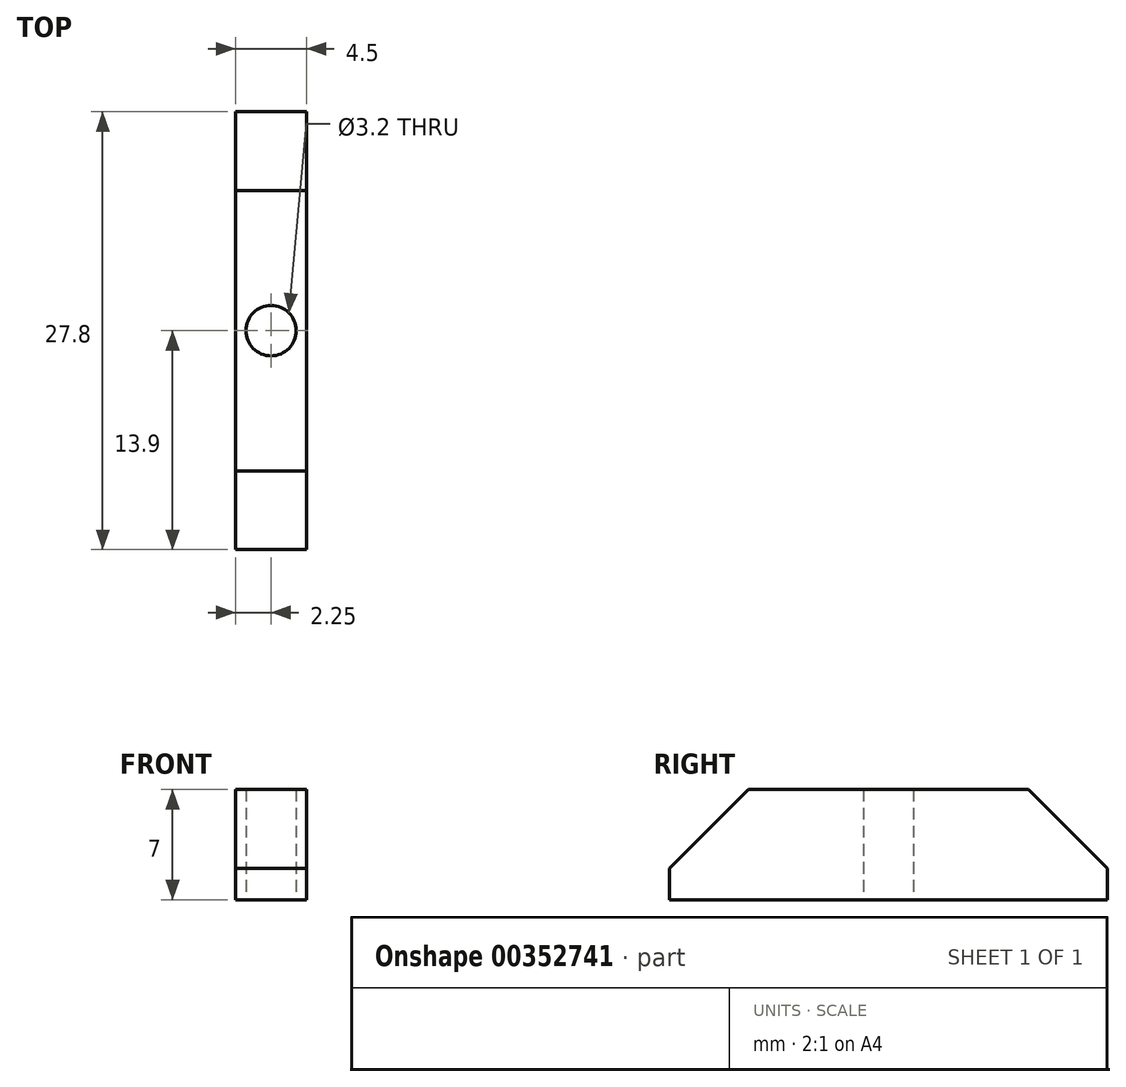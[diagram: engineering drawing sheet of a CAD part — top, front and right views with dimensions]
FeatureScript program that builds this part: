
annotation { "Feature Type Name" : "Feature", "Feature Type Description" : "" }
export const myFeature = defineFeature(function(context is Context, id is Id, definition is map)
    precondition{}
    {
        {
            var Q0;
            Q0=qCreatedBy(makeId("Top.planeOp"),FACE);
            var sketch = newSketch(context, id + "F0", { "sketchPlane" : qUnion([Q0])});
            skLineSegment(sketch, "E0.bottom", {"start": v(2.25, 13.9) * mm, "end": v(-2.25, 13.9) * mm});
            skLineSegment(sketch, "E0.top", {"start": v(2.25, -13.9) * mm, "end": v(-2.25, -13.9) * mm});
            skLineSegment(sketch, "E0.left", {"start": v(2.25, 13.9) * mm, "end": v(2.25, -13.9) * mm});
            skLineSegment(sketch, "E0.right", {"start": v(-2.25, 13.9) * mm, "end": v(-2.25, -13.9) * mm});
            skPoint(sketch, "E0.middle", {"position": v(0, 0) * mm});
            skCircle(sketch, "E1", {"center": v(0, 0) * mm, "radius": 1.6 * mm});
            skSolve(sketch);
        }
        {
            var Q0;
            Q0=makeQuery(id+"F0.imprint","IMPRINT",FACE,{"disambiguationData":[TD([[makeQuery(id+"F0.imprint","IMPRINT",EDGE,{"derivedFrom":sQuery(id+"F0.wireOp",EDGE,"E0.bottom")}),1.0]])]});
            extrude(context, id + "F1", {"entities" : qUnion([Q0]), "depth" : 7 * mm});
        }
        {
            var Q0;
            Q0=makeQuery(id+"F1.opExtrude","CAP_EDGE",EDGE,{"disambiguationData":[OSD([sQuery(id+"F0.wireOp",EDGE,"E0.top")])],"isStart":false});
            var Q1;
            Q1=makeQuery(id+"F1.opExtrude","CAP_EDGE",EDGE,{"disambiguationData":[OSD([sQuery(id+"F0.wireOp",EDGE,"E0.bottom")])],"isStart":false});
            chamfer(context, id + "F2", {"entities" : qUnion([Q0, Q1]), "width" : 5 * mm, "tangentPropagation" : true});
        }
    });
